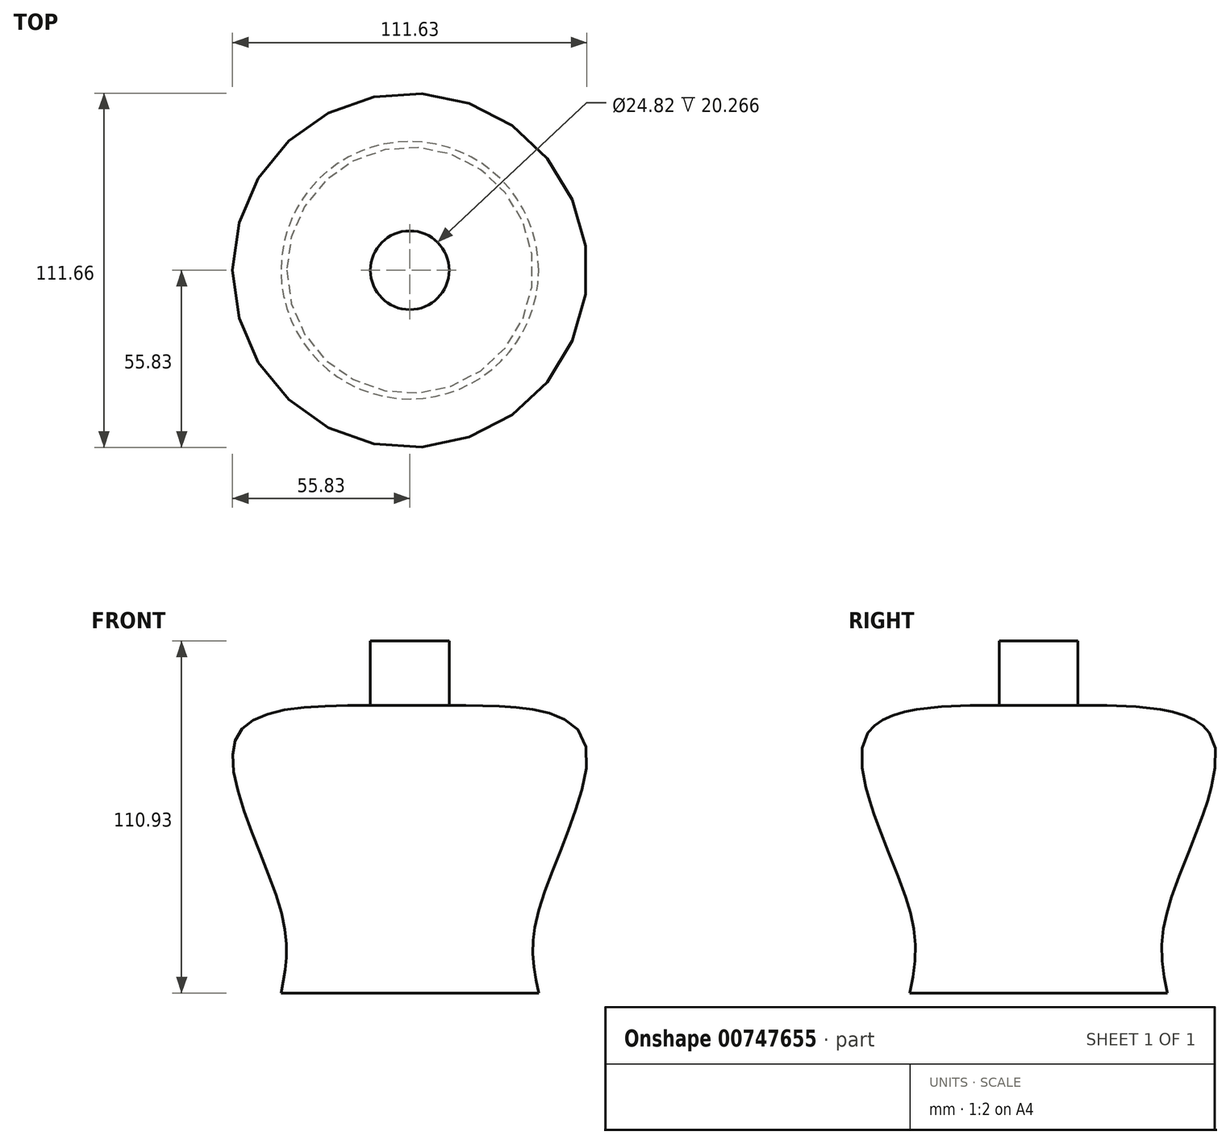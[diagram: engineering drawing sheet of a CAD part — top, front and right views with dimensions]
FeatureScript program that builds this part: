
annotation { "Feature Type Name" : "Feature", "Feature Type Description" : "" }
export const myFeature = defineFeature(function(context is Context, id is Id, definition is map)
    precondition{}
    {
        {
            var Q0;
            Q0=qCreatedBy(makeId("Front.planeOp"),FACE);
            var sketch = newSketch(context, id + "F0", { "sketchPlane" : qUnion([Q0])});
            skLineSegment(sketch, "E0", {"start": v(12.41, 50.83) * mm, "end": v(0, 50.83) * mm});
            skLineSegment(sketch, "E1", {"start": v(0, 50.83) * mm, "end": v(0, -60.1) * mm});
            skLineSegment(sketch, "E2", {"start": v(0, -60.1) * mm, "end": v(40.57, -60.1) * mm});
            skLineSegment(sketch, "E3", {"start": v(12.41, 50.83) * mm, "end": v(12.41, 30.57) * mm});
            skFitSpline(sketch, "E4", {"points": [v(12.41, 30.57) * mm, v(54.91, 19.75) * mm, v(40.53, -34.38) * mm, v(40.57, -60.1) * mm], "startDerivative": vector(166.65, -0.8) * mm, "endDerivative": vector(17.56, -81.92) * mm});
            skSolve(sketch);
        }
        {
            var Q0;
            Q0=sQuery(id+"F0.wireOp",EDGE,"E2");
            var Q1;
            Q1=sQuery(id+"F0.wireOp",EDGE,"E3");
            var Q2;
            Q2=sQuery(id+"F0.wireOp",EDGE,"E0");
            var Q3;
            Q3=sQuery(id+"F0.wireOp",EDGE,"E4");
            var Q4;
            Q4=sQuery(id+"F0.wireOp",EDGE,"E1");
            revolve(context, id + "F1", {"bodyType" : ToolBodyType.SURFACE, "surfaceOperationType" : NewSurfaceOperationType.NEW, "surfaceEntities" : qUnion([Q0, Q1, Q2, Q3]), "axis" : qUnion([Q4]), "revolveType" : RevolveType.FULL});
        }
    });
